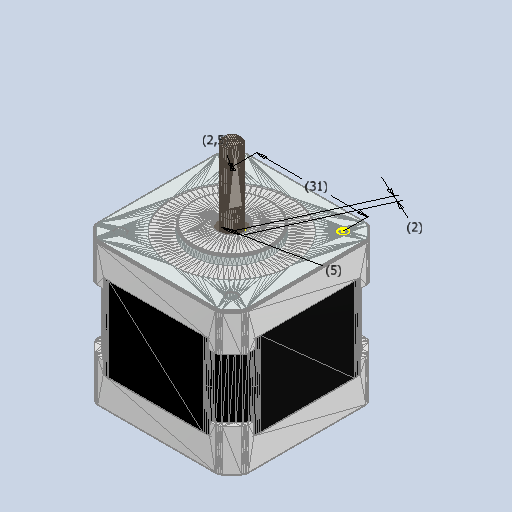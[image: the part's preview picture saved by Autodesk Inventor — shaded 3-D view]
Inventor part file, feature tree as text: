
AUTODESK INVENTOR PART (.ipt)
format: ipt  version: 2022.2 (Build 262287000, 287)  size: 1,188,352 bytes
history: native  units: mm
features: other x2, sketch x1
ambient origin geometry x8: Origin, YZ Plane, XZ Plane, XY Plane, X Axis, Y Axis, Z Axis, Center Point
feature tree (3):
  other  "17HM15-0904S"
  sketch  "Sketch1"
  other  "MeshFeature1"
